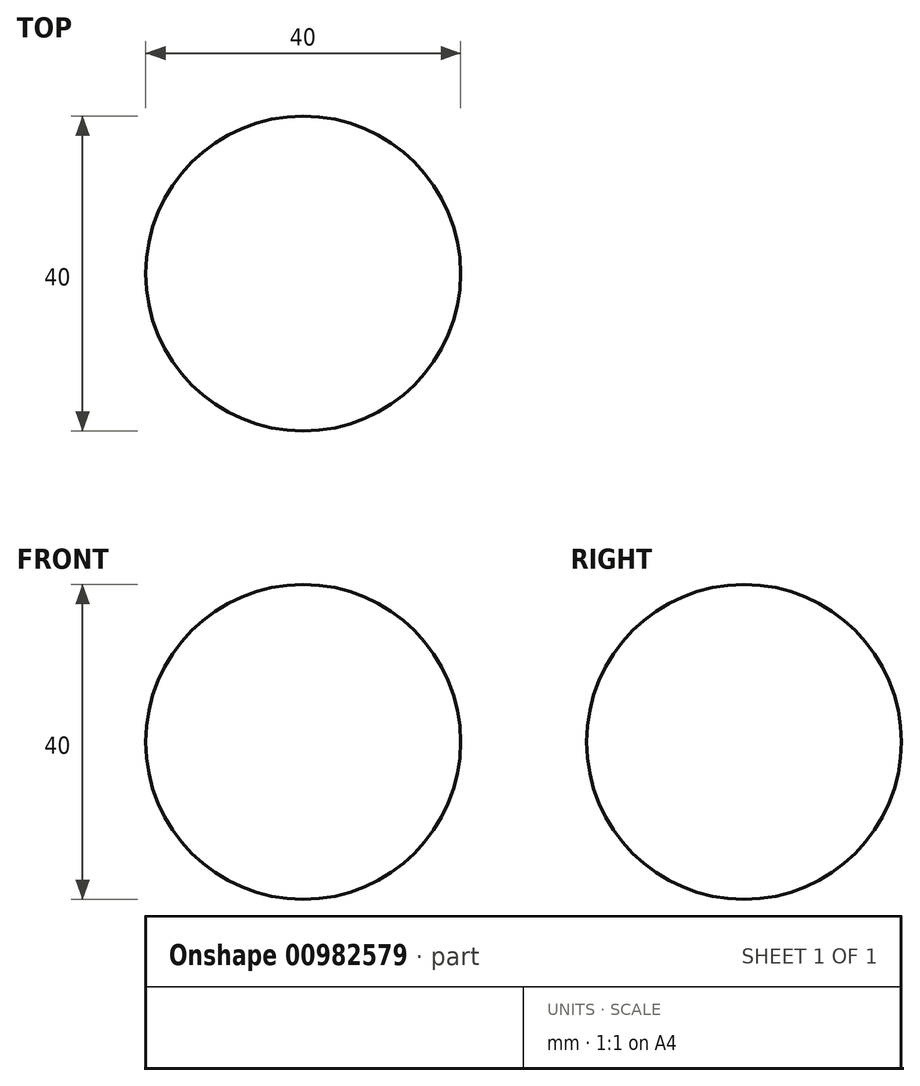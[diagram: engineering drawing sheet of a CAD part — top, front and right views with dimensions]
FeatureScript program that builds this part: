
annotation { "Feature Type Name" : "Feature", "Feature Type Description" : "" }
export const myFeature = defineFeature(function(context is Context, id is Id, definition is map)
    precondition{}
    {
        {
            var Q0;
            Q0=qCreatedBy(makeId("Front.planeOp"),FACE);
            var sketch = newSketch(context, id + "F0", { "sketchPlane" : qUnion([Q0])});
            skLineSegment(sketch, "E0", {"start": v(0, 0) * mm, "end": v(0, 20) * mm});
            skLineSegment(sketch, "E1", {"start": v(0, 0) * mm, "end": v(0, -20.17) * mm});
            skArc(sketch, "E2", {"start": v(0, 20) * mm, "mid": v(-20, 0) * mm, "end": v(0, -20) * mm});
            skLineSegment(sketch, "E3", {"start": v(0, 0) * mm, "end": v(0, -20) * mm});
            skSolve(sketch);
        }
        {
            var Q0;
            Q0 = qSketchRegion(id + "F0", true);
            var Q1;
            Q1=sQuery(id+"F0.wireOp",EDGE,"E0");
            revolve(context, id + "F1", {"surfaceOperationType" : NewSurfaceOperationType.NEW, "entities" : qUnion([Q0]), "axis" : qUnion([Q1]), "revolveType" : RevolveType.FULL});
        }
    });
